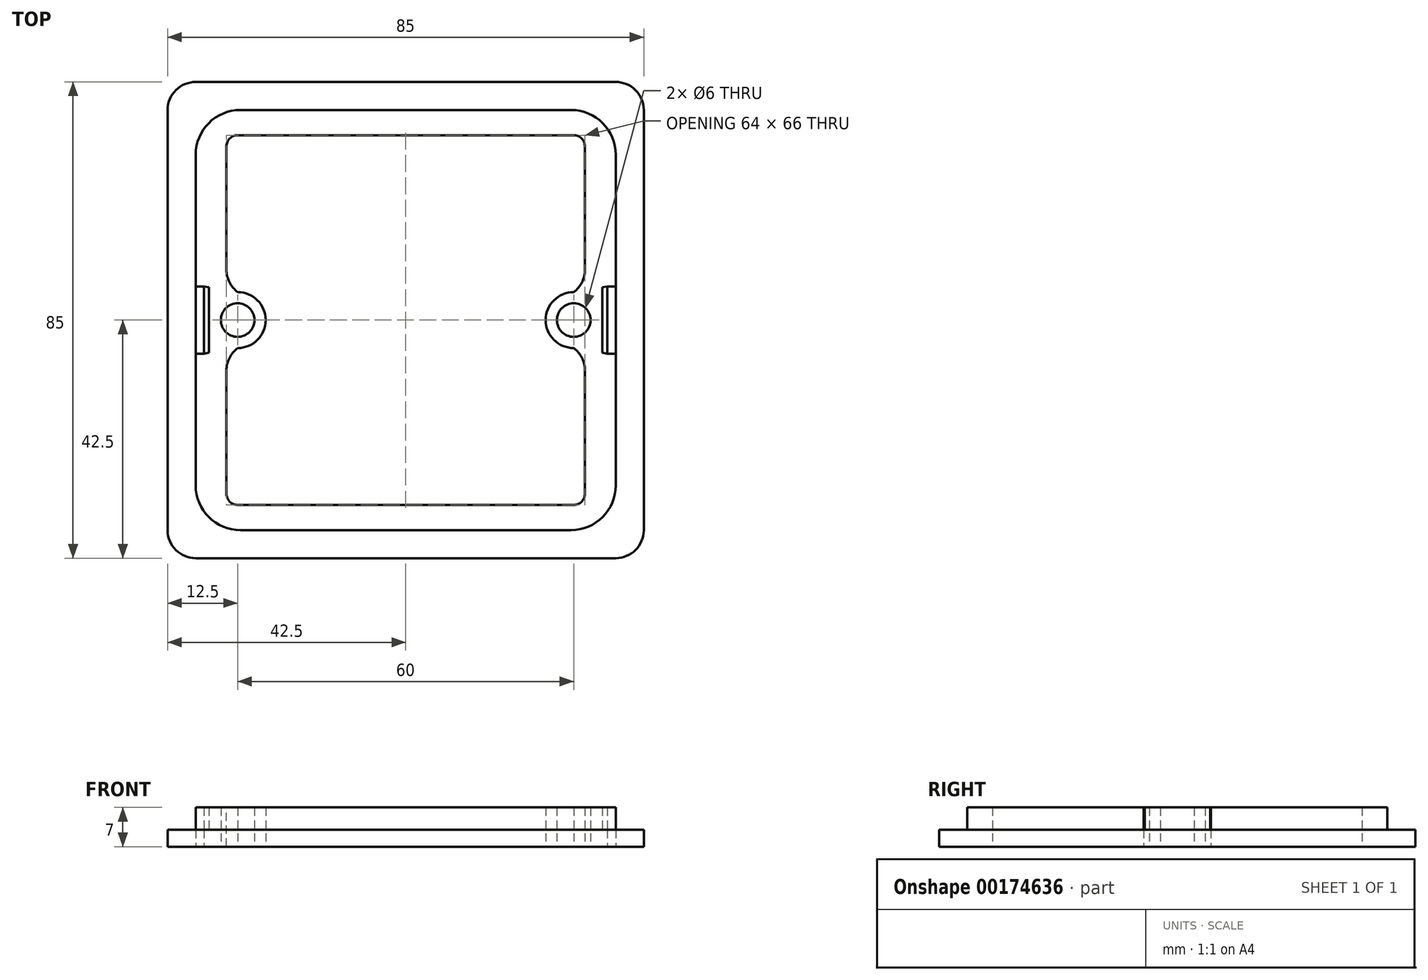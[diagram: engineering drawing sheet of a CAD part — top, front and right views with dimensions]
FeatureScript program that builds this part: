
annotation { "Feature Type Name" : "Feature", "Feature Type Description" : "" }
export const myFeature = defineFeature(function(context is Context, id is Id, definition is map)
    precondition{}
    {
        {
            var Q0;
            Q0=qCreatedBy(makeId("Top.planeOp"),FACE);
            var sketch = newSketch(context, id + "F0", { "sketchPlane" : qUnion([Q0])});
            skLineSegment(sketch, "E0.bottom", {"start": v(-42.5, 42.5) * mm, "end": v(42.5, 42.5) * mm});
            skLineSegment(sketch, "E0.top", {"start": v(-42.5, -42.5) * mm, "end": v(42.5, -42.5) * mm});
            skLineSegment(sketch, "E0.left", {"start": v(-42.5, 42.5) * mm, "end": v(-42.5, -42.5) * mm});
            skLineSegment(sketch, "E0.right", {"start": v(42.5, 42.5) * mm, "end": v(42.5, -42.5) * mm});
            skLineSegment(sketch, "E1.bottom", {"start": v(-32, 33) * mm, "end": v(32, 33) * mm});
            skLineSegment(sketch, "E1.top", {"start": v(-32, -33) * mm, "end": v(32, -33) * mm});
            skLineSegment(sketch, "E1.left", {"start": v(-32, 33) * mm, "end": v(-32, -33) * mm});
            skLineSegment(sketch, "E1.right", {"start": v(32, 33) * mm, "end": v(32, -33) * mm});
            skPoint(sketch, "E2", {"position": v(0, 33) * mm});
            skPoint(sketch, "E3", {"position": v(-42.5, 0) * mm});
            skPoint(sketch, "E4", {"position": v(-32, 0) * mm});
            skPoint(sketch, "E5", {"position": v(0, 42.5) * mm});
            skLineSegment(sketch, "E6.bottom", {"start": v(37.5, -37.5) * mm, "end": v(-37.5, -37.5) * mm});
            skLineSegment(sketch, "E6.top", {"start": v(37.5, 37.5) * mm, "end": v(-37.5, 37.5) * mm});
            skLineSegment(sketch, "E6.left", {"start": v(37.5, -37.5) * mm, "end": v(37.5, 37.5) * mm});
            skLineSegment(sketch, "E6.right", {"start": v(-37.5, -37.5) * mm, "end": v(-37.5, 37.5) * mm});
            skPoint(sketch, "E6.middle", {"position": v(0, 0) * mm});
            skCircle(sketch, "E7", {"center": v(-30, 0) * mm, "radius": 3 * mm});
            skLineSegment(sketch, "E8.bottom", {"start": v(35.1, 35.1) * mm, "end": v(-35.1, 35.1) * mm});
            skLineSegment(sketch, "E8.top", {"start": v(35.1, -35.1) * mm, "end": v(-35.1, -35.1) * mm});
            skLineSegment(sketch, "E8.left", {"start": v(35.1, 35.1) * mm, "end": v(35.1, -35.1) * mm});
            skLineSegment(sketch, "E8.right", {"start": v(-35.1, 35.1) * mm, "end": v(-35.1, -35.1) * mm});
            skLineSegment(sketch, "E9", {"start": v(0, 0) * mm, "end": v(0, 30.07) * mm});
            skCircle(sketch, "E10.MirrorC", {"center": v(30, 0) * mm, "radius": 3 * mm});
            skLineSegment(sketch, "E11.bottom", {"start": v(-37.5, 6) * mm, "end": v(-36, 6) * mm});
            skLineSegment(sketch, "E11.top", {"start": v(-37.5, -6) * mm, "end": v(-36, -6) * mm});
            skLineSegment(sketch, "E11.left", {"start": v(-37.5, 6) * mm, "end": v(-37.5, -6) * mm});
            skLineSegment(sketch, "E11.right", {"start": v(-36, 6) * mm, "end": v(-36, -6) * mm});
            skPoint(sketch, "E12", {"position": v(-36, 0) * mm});
            skLineSegment(sketch, "E13.MirrorCS", {"start": v(37.5, 6) * mm, "end": v(36, 6) * mm});
            skLineSegment(sketch, "E14.MirrorCS", {"start": v(37.5, -6) * mm, "end": v(36, -6) * mm});
            skLineSegment(sketch, "E15.MirrorCS", {"start": v(36, 6) * mm, "end": v(36, -6) * mm});
            skLineSegment(sketch, "E16.MirrorCS", {"start": v(37.5, 6) * mm, "end": v(37.5, -6) * mm});
            skCircle(sketch, "E17", {"center": v(-30, 0) * mm, "radius": 5 * mm});
            skLineSegment(sketch, "E18", {"start": v(-30, 5) * mm, "end": v(-36, 6) * mm});
            skLineSegment(sketch, "E19", {"start": v(-30, -5) * mm, "end": v(-36, -6) * mm});
            skLineSegment(sketch, "E20.MirrorCS", {"start": v(30, 5) * mm, "end": v(36, 6) * mm});
            skLineSegment(sketch, "E21.MirrorCS", {"start": v(30, -5) * mm, "end": v(36, -6) * mm});
            skCircle(sketch, "E22.MirrorC", {"center": v(30, 0) * mm, "radius": 5 * mm});
            skSolve(sketch);
        }
        {
            var Q0;
            Q0=makeQuery(id+"F0.imprint","IMPRINT",FACE,{"disambiguationData":[TD([[makeQuery(id+"F0.imprint","IMPRINT",EDGE,{"derivedFrom":sQuery(id+"F0.wireOp",EDGE,"E0.bottom")}),-1.0]])]});
            var Q1;
            {var subQ4=sQuery(id+"F0.wireOp",EDGE,"E6.bottom");Q1=makeQuery(id+"F0.imprint","IMPRINT",FACE,{"disambiguationData":[TD([[makeQuery(id+"F0.imprint","IMPRINT",EDGE,{"derivedFrom":subQ4}),-1.0]])]});}
            var Q2;
            {var subQ1=sQuery(id+"F0.wireOp",EDGE,"E6.top");Q2=makeQuery(id+"F0.imprint","IMPRINT",FACE,{"disambiguationData":[TD([[makeQuery(id+"F0.imprint","IMPRINT",EDGE,{"derivedFrom":subQ1}),1.0]])]});}
            var Q3;
            {var subQ2=sQuery(id+"F0.wireOp",EDGE,"E1.bottom");Q3=makeQuery(id+"F0.imprint","IMPRINT",FACE,{"disambiguationData":[TD([[makeQuery(id+"F0.imprint","IMPRINT",EDGE,{"derivedFrom":subQ2}),1.0]])]});}
            var Q4;
            {var subQ1=sQuery(id+"F0.wireOp",EDGE,"E1.left");var subQ8=sQuery(id+"F0.wireOp",EDGE,"E18");var subQ10=makeQuery(id+"F0.imprint","INTERSECT",VERTEX,{"derivedFrom":[subQ1,subQ8]});Q4=makeQuery(id+"F0.imprint","IMPRINT",FACE,{"disambiguationData":[TD([[makeQuery(id+"F0.imprint","IMPRINT",EDGE,{"disambiguationData":[TD([[subQ10,-1.0]])],"derivedFrom":subQ1}),-1.0]])]});}
            var Q5;
            {var subQ5=sQuery(id+"F0.wireOp",EDGE,"E11.right");Q5=makeQuery(id+"F0.imprint","IMPRINT",FACE,{"disambiguationData":[TD([[makeQuery(id+"F0.imprint","IMPRINT",EDGE,{"derivedFrom":subQ5}),1.0]])]});}
            var Q6;
            {var subQ0=sQuery(id+"F0.wireOp",EDGE,"E17");var subQ2=sQuery(id+"F0.wireOp",EDGE,"E1.left");var subQ3=makeQuery(id+"F0.imprint","INTERSECT",VERTEX,{"disambiguationData":[OD(0.0)],"derivedFrom":[subQ2,subQ0]});Q6=makeQuery(id+"F0.imprint","IMPRINT",FACE,{"disambiguationData":[TD([[makeQuery(id+"F0.imprint","IMPRINT",EDGE,{"disambiguationData":[TD([[subQ3,-1.0]])],"derivedFrom":subQ2}),1.0]])]});}
            var Q7;
            {var subQ0=sQuery(id+"F0.wireOp",EDGE,"E18");var subQ1=sQuery(id+"F0.wireOp",EDGE,"E1.left");var subQ2=makeQuery(id+"F0.imprint","INTERSECT",VERTEX,{"derivedFrom":[subQ1,subQ0]});Q7=makeQuery(id+"F0.imprint","IMPRINT",FACE,{"disambiguationData":[TD([[makeQuery(id+"F0.imprint","IMPRINT",EDGE,{"disambiguationData":[TD([[subQ2,-1.0]])],"derivedFrom":subQ1}),1.0]])]});}
            var Q8;
            {var subQ0=sQuery(id+"F0.wireOp",EDGE,"E17");var subQ1=sQuery(id+"F0.wireOp",EDGE,"E1.left");var subQ2=makeQuery(id+"F0.imprint","INTERSECT",VERTEX,{"disambiguationData":[OD(1.0)],"derivedFrom":[subQ1,subQ0]});Q8=makeQuery(id+"F0.imprint","IMPRINT",FACE,{"disambiguationData":[TD([[makeQuery(id+"F0.imprint","IMPRINT",EDGE,{"disambiguationData":[TD([[subQ2,-1.0]])],"derivedFrom":subQ1}),1.0]])]});}
            var Q9;
            {var subQ11=sQuery(id+"F0.wireOp",EDGE,"E1.top");Q9=makeQuery(id+"F0.imprint","IMPRINT",FACE,{"disambiguationData":[TD([[makeQuery(id+"F0.imprint","IMPRINT",EDGE,{"derivedFrom":subQ11}),-1.0]])]});}
            var Q10;
            {var subQ0=sQuery(id+"F0.wireOp",EDGE,"E20.MirrorCS");var subQ6=sQuery(id+"F0.wireOp",EDGE,"E1.right");var subQ9=makeQuery(id+"F0.imprint","INTERSECT",VERTEX,{"derivedFrom":[subQ6,subQ0]});Q10=makeQuery(id+"F0.imprint","IMPRINT",FACE,{"disambiguationData":[TD([[makeQuery(id+"F0.imprint","IMPRINT",EDGE,{"disambiguationData":[TD([[subQ9,-1.0]])],"derivedFrom":subQ6}),1.0]])]});}
            var Q11;
            {var subQ0=sQuery(id+"F0.wireOp",EDGE,"E20.MirrorCS");var subQ1=sQuery(id+"F0.wireOp",EDGE,"E1.right");var subQ2=makeQuery(id+"F0.imprint","INTERSECT",VERTEX,{"derivedFrom":[subQ1,subQ0]});Q11=makeQuery(id+"F0.imprint","IMPRINT",FACE,{"disambiguationData":[TD([[makeQuery(id+"F0.imprint","IMPRINT",EDGE,{"disambiguationData":[TD([[subQ2,-1.0]])],"derivedFrom":subQ1}),-1.0]])]});}
            var Q12;
            {var subQ0=sQuery(id+"F0.wireOp",EDGE,"E22.MirrorC");var subQ1=sQuery(id+"F0.wireOp",EDGE,"E1.right");var subQ2=makeQuery(id+"F0.imprint","INTERSECT",VERTEX,{"disambiguationData":[OD(1.0)],"derivedFrom":[subQ1,subQ0]});Q12=makeQuery(id+"F0.imprint","IMPRINT",FACE,{"disambiguationData":[TD([[makeQuery(id+"F0.imprint","IMPRINT",EDGE,{"disambiguationData":[TD([[subQ2,-1.0]])],"derivedFrom":subQ1}),-1.0]])]});}
            var Q13;
            {var subQ0=sQuery(id+"F0.wireOp",EDGE,"E22.MirrorC");var subQ2=sQuery(id+"F0.wireOp",EDGE,"E1.right");var subQ3=makeQuery(id+"F0.imprint","INTERSECT",VERTEX,{"disambiguationData":[OD(0.0)],"derivedFrom":[subQ2,subQ0]});Q13=makeQuery(id+"F0.imprint","IMPRINT",FACE,{"disambiguationData":[TD([[makeQuery(id+"F0.imprint","IMPRINT",EDGE,{"disambiguationData":[TD([[subQ3,-1.0]])],"derivedFrom":subQ2}),-1.0]])]});}
            var Q14;
            {var subQ0=sQuery(id+"F0.wireOp",EDGE,"E22.MirrorC");var subQ1=sQuery(id+"F0.wireOp",EDGE,"E1.right");var subQ2=makeQuery(id+"F0.imprint","INTERSECT",VERTEX,{"disambiguationData":[OD(0.0)],"derivedFrom":[subQ1,subQ0]});Q14=makeQuery(id+"F0.imprint","IMPRINT",FACE,{"disambiguationData":[TD([[makeQuery(id+"F0.imprint","IMPRINT",EDGE,{"disambiguationData":[TD([[subQ2,-1.0]])],"derivedFrom":subQ1}),1.0]])]});}
            var Q15;
            {var subQ0=sQuery(id+"F0.wireOp",EDGE,"E17");var subQ1=sQuery(id+"F0.wireOp",EDGE,"E1.left");var subQ2=makeQuery(id+"F0.imprint","INTERSECT",VERTEX,{"disambiguationData":[OD(0.0)],"derivedFrom":[subQ1,subQ0]});Q15=makeQuery(id+"F0.imprint","IMPRINT",FACE,{"disambiguationData":[TD([[makeQuery(id+"F0.imprint","IMPRINT",EDGE,{"disambiguationData":[TD([[subQ2,-1.0]])],"derivedFrom":subQ1}),-1.0]])]});}
            var Q16;
            {var subQ5=sQuery(id+"F0.wireOp",EDGE,"E15.MirrorCS");Q16=makeQuery(id+"F0.imprint","IMPRINT",FACE,{"disambiguationData":[TD([[makeQuery(id+"F0.imprint","IMPRINT",EDGE,{"derivedFrom":subQ5}),-1.0]])]});}
            extrude(context, id + "F1", {"entities" : qUnion([Q0, Q1, Q2, Q3, Q4, Q5, Q6, Q7, Q8, Q9, Q10, Q11, Q12, Q13, Q14, Q15, Q16]), "depth" : 3 * mm});
        }
        {
            var Q0;
            Q0=makeQuery(id+"F1.opExtrude","SWEPT_EDGE",EDGE,{"disambiguationData":[OSD([sQuery(id+"F0.wireOp",EDGE,"E0.bottom"),sQuery(id+"F0.wireOp",EDGE,"E0.left")])]});
            var Q1;
            Q1=makeQuery(id+"F1.opExtrude","SWEPT_EDGE",EDGE,{"disambiguationData":[OSD([sQuery(id+"F0.wireOp",EDGE,"E0.top"),sQuery(id+"F0.wireOp",EDGE,"E0.left")])]});
            var Q2;
            Q2=makeQuery(id+"F1.opExtrude","SWEPT_EDGE",EDGE,{"disambiguationData":[OSD([sQuery(id+"F0.wireOp",EDGE,"E0.top"),sQuery(id+"F0.wireOp",EDGE,"E0.right")])]});
            var Q3;
            Q3=makeQuery(id+"F1.opExtrude","SWEPT_EDGE",EDGE,{"disambiguationData":[OSD([sQuery(id+"F0.wireOp",EDGE,"E0.bottom"),sQuery(id+"F0.wireOp",EDGE,"E0.right")])]});
            fillet(context, id + "F2", {"entities" : qUnion([Q0, Q1, Q2, Q3]), "radius" : 5 * mm, "tangentPropagation" : true, "allowEdgeOverflow" : false});
        }
        {
            var Q0;
            {var subQ1=sQuery(id+"F0.wireOp",EDGE,"E1.left");var subQ8=sQuery(id+"F0.wireOp",EDGE,"E18");var subQ10=makeQuery(id+"F0.imprint","INTERSECT",VERTEX,{"derivedFrom":[subQ1,subQ8]});Q0=makeQuery(id+"F0.imprint","IMPRINT",FACE,{"disambiguationData":[TD([[makeQuery(id+"F0.imprint","IMPRINT",EDGE,{"disambiguationData":[TD([[subQ10,-1.0]])],"derivedFrom":subQ1}),-1.0]])]});}
            var Q1;
            {var subQ0=sQuery(id+"F0.wireOp",EDGE,"E18");var subQ1=sQuery(id+"F0.wireOp",EDGE,"E1.left");var subQ2=makeQuery(id+"F0.imprint","INTERSECT",VERTEX,{"derivedFrom":[subQ1,subQ0]});Q1=makeQuery(id+"F0.imprint","IMPRINT",FACE,{"disambiguationData":[TD([[makeQuery(id+"F0.imprint","IMPRINT",EDGE,{"disambiguationData":[TD([[subQ2,-1.0]])],"derivedFrom":subQ1}),1.0]])]});}
            var Q2;
            {var subQ0=sQuery(id+"F0.wireOp",EDGE,"E17");var subQ2=sQuery(id+"F0.wireOp",EDGE,"E1.left");var subQ3=makeQuery(id+"F0.imprint","INTERSECT",VERTEX,{"disambiguationData":[OD(0.0)],"derivedFrom":[subQ2,subQ0]});Q2=makeQuery(id+"F0.imprint","IMPRINT",FACE,{"disambiguationData":[TD([[makeQuery(id+"F0.imprint","IMPRINT",EDGE,{"disambiguationData":[TD([[subQ3,-1.0]])],"derivedFrom":subQ2}),1.0]])]});}
            var Q3;
            {var subQ0=sQuery(id+"F0.wireOp",EDGE,"E17");var subQ1=sQuery(id+"F0.wireOp",EDGE,"E1.left");var subQ2=makeQuery(id+"F0.imprint","INTERSECT",VERTEX,{"disambiguationData":[OD(0.0)],"derivedFrom":[subQ1,subQ0]});Q3=makeQuery(id+"F0.imprint","IMPRINT",FACE,{"disambiguationData":[TD([[makeQuery(id+"F0.imprint","IMPRINT",EDGE,{"disambiguationData":[TD([[subQ2,-1.0]])],"derivedFrom":subQ1}),-1.0]])]});}
            var Q4;
            {var subQ0=sQuery(id+"F0.wireOp",EDGE,"E17");var subQ1=sQuery(id+"F0.wireOp",EDGE,"E1.left");var subQ2=makeQuery(id+"F0.imprint","INTERSECT",VERTEX,{"disambiguationData":[OD(1.0)],"derivedFrom":[subQ1,subQ0]});Q4=makeQuery(id+"F0.imprint","IMPRINT",FACE,{"disambiguationData":[TD([[makeQuery(id+"F0.imprint","IMPRINT",EDGE,{"disambiguationData":[TD([[subQ2,-1.0]])],"derivedFrom":subQ1}),1.0]])]});}
            var Q5;
            {var subQ11=sQuery(id+"F0.wireOp",EDGE,"E1.top");Q5=makeQuery(id+"F0.imprint","IMPRINT",FACE,{"disambiguationData":[TD([[makeQuery(id+"F0.imprint","IMPRINT",EDGE,{"derivedFrom":subQ11}),-1.0]])]});}
            var Q6;
            {var subQ2=sQuery(id+"F0.wireOp",EDGE,"E6.bottom");Q6=makeQuery(id+"F0.imprint","IMPRINT",FACE,{"disambiguationData":[TD([[makeQuery(id+"F0.imprint","IMPRINT",EDGE,{"derivedFrom":subQ2}),-1.0]])]});}
            var Q7;
            {var subQ1=sQuery(id+"F0.wireOp",EDGE,"E6.top");Q7=makeQuery(id+"F0.imprint","IMPRINT",FACE,{"disambiguationData":[TD([[makeQuery(id+"F0.imprint","IMPRINT",EDGE,{"derivedFrom":subQ1}),1.0]])]});}
            var Q8;
            {var subQ2=sQuery(id+"F0.wireOp",EDGE,"E1.bottom");Q8=makeQuery(id+"F0.imprint","IMPRINT",FACE,{"disambiguationData":[TD([[makeQuery(id+"F0.imprint","IMPRINT",EDGE,{"derivedFrom":subQ2}),1.0]])]});}
            var Q9;
            {var subQ0=sQuery(id+"F0.wireOp",EDGE,"E22.MirrorC");var subQ1=sQuery(id+"F0.wireOp",EDGE,"E1.right");var subQ2=makeQuery(id+"F0.imprint","INTERSECT",VERTEX,{"disambiguationData":[OD(1.0)],"derivedFrom":[subQ1,subQ0]});Q9=makeQuery(id+"F0.imprint","IMPRINT",FACE,{"disambiguationData":[TD([[makeQuery(id+"F0.imprint","IMPRINT",EDGE,{"disambiguationData":[TD([[subQ2,-1.0]])],"derivedFrom":subQ1}),-1.0]])]});}
            var Q10;
            {var subQ0=sQuery(id+"F0.wireOp",EDGE,"E22.MirrorC");var subQ2=sQuery(id+"F0.wireOp",EDGE,"E1.right");var subQ3=makeQuery(id+"F0.imprint","INTERSECT",VERTEX,{"disambiguationData":[OD(0.0)],"derivedFrom":[subQ2,subQ0]});Q10=makeQuery(id+"F0.imprint","IMPRINT",FACE,{"disambiguationData":[TD([[makeQuery(id+"F0.imprint","IMPRINT",EDGE,{"disambiguationData":[TD([[subQ3,-1.0]])],"derivedFrom":subQ2}),-1.0]])]});}
            var Q11;
            {var subQ0=sQuery(id+"F0.wireOp",EDGE,"E20.MirrorCS");var subQ1=sQuery(id+"F0.wireOp",EDGE,"E1.right");var subQ2=makeQuery(id+"F0.imprint","INTERSECT",VERTEX,{"derivedFrom":[subQ1,subQ0]});Q11=makeQuery(id+"F0.imprint","IMPRINT",FACE,{"disambiguationData":[TD([[makeQuery(id+"F0.imprint","IMPRINT",EDGE,{"disambiguationData":[TD([[subQ2,-1.0]])],"derivedFrom":subQ1}),-1.0]])]});}
            var Q12;
            {var subQ0=sQuery(id+"F0.wireOp",EDGE,"E22.MirrorC");var subQ1=sQuery(id+"F0.wireOp",EDGE,"E1.right");var subQ2=makeQuery(id+"F0.imprint","INTERSECT",VERTEX,{"disambiguationData":[OD(0.0)],"derivedFrom":[subQ1,subQ0]});Q12=makeQuery(id+"F0.imprint","IMPRINT",FACE,{"disambiguationData":[TD([[makeQuery(id+"F0.imprint","IMPRINT",EDGE,{"disambiguationData":[TD([[subQ2,-1.0]])],"derivedFrom":subQ1}),1.0]])]});}
            var Q13;
            {var subQ0=sQuery(id+"F0.wireOp",EDGE,"E20.MirrorCS");var subQ6=sQuery(id+"F0.wireOp",EDGE,"E1.right");var subQ9=makeQuery(id+"F0.imprint","INTERSECT",VERTEX,{"derivedFrom":[subQ6,subQ0]});Q13=makeQuery(id+"F0.imprint","IMPRINT",FACE,{"disambiguationData":[TD([[makeQuery(id+"F0.imprint","IMPRINT",EDGE,{"disambiguationData":[TD([[subQ9,-1.0]])],"derivedFrom":subQ6}),1.0]])]});}
            extrude(context, id + "F3", {"entities" : qUnion([Q0, Q1, Q2, Q3, Q4, Q5, Q6, Q7, Q8, Q9, Q10, Q11, Q12, Q13]), "operationType" : NewBodyOperationType.ADD, "depth" : 7 * mm});
        }
        {
            var Q0;
            Q0=makeQuery(id+"F3.opExtrude","SWEPT_EDGE",EDGE,{"disambiguationData":[OSD([sQuery(id+"F0.wireOp",EDGE,"E6.bottom"),sQuery(id+"F0.wireOp",EDGE,"E6.right")])]});
            var Q1;
            Q1=makeQuery(id+"F3.opExtrude","SWEPT_EDGE",EDGE,{"disambiguationData":[OSD([sQuery(id+"F0.wireOp",EDGE,"E6.bottom"),sQuery(id+"F0.wireOp",EDGE,"E6.left")])]});
            var Q2;
            Q2=makeQuery(id+"F3.opExtrude","SWEPT_EDGE",EDGE,{"disambiguationData":[OSD([sQuery(id+"F0.wireOp",EDGE,"E6.top"),sQuery(id+"F0.wireOp",EDGE,"E6.left")])]});
            var Q3;
            Q3=makeQuery(id+"F3.opExtrude","SWEPT_EDGE",EDGE,{"disambiguationData":[OSD([sQuery(id+"F0.wireOp",EDGE,"E6.top"),sQuery(id+"F0.wireOp",EDGE,"E6.right")])]});
            fillet(context, id + "F4", {"entities" : qUnion([Q0, Q1, Q2, Q3]), "radius" : 8 * mm, "tangentPropagation" : true, "allowEdgeOverflow" : false});
        }
        {
            var Q0;
            {var subQ0=sQuery(id+"F0.wireOp",EDGE,"E1.right");var subQ1=sQuery(id+"F0.wireOp",EDGE,"E1.top");Q0=makeQuery(id+"F3.boolean.opBoolean","MERGE",EDGE,{"derivedFrom":[makeQuery(id+"F1.opExtrude","SWEPT_EDGE",EDGE,{"disambiguationData":[OSD([subQ1,subQ0])]}),makeQuery(id+"F3.opExtrude","SWEPT_EDGE",EDGE,{"disambiguationData":[OSD([subQ1,subQ0])]})]});}
            var Q1;
            {var subQ0=sQuery(id+"F0.wireOp",EDGE,"E1.left");var subQ1=sQuery(id+"F0.wireOp",EDGE,"E1.top");Q1=makeQuery(id+"F3.boolean.opBoolean","MERGE",EDGE,{"derivedFrom":[makeQuery(id+"F1.opExtrude","SWEPT_EDGE",EDGE,{"disambiguationData":[OSD([subQ1,subQ0])]}),makeQuery(id+"F3.opExtrude","SWEPT_EDGE",EDGE,{"disambiguationData":[OSD([subQ1,subQ0])]})]});}
            var Q2;
            {var subQ0=sQuery(id+"F0.wireOp",EDGE,"E1.left");var subQ1=sQuery(id+"F0.wireOp",EDGE,"E1.bottom");Q2=makeQuery(id+"F3.boolean.opBoolean","MERGE",EDGE,{"derivedFrom":[makeQuery(id+"F1.opExtrude","SWEPT_EDGE",EDGE,{"disambiguationData":[OSD([subQ1,subQ0])]}),makeQuery(id+"F3.opExtrude","SWEPT_EDGE",EDGE,{"disambiguationData":[OSD([subQ1,subQ0])]})]});}
            var Q3;
            {var subQ0=sQuery(id+"F0.wireOp",EDGE,"E1.right");var subQ1=sQuery(id+"F0.wireOp",EDGE,"E1.bottom");Q3=makeQuery(id+"F3.boolean.opBoolean","MERGE",EDGE,{"derivedFrom":[makeQuery(id+"F1.opExtrude","SWEPT_EDGE",EDGE,{"disambiguationData":[OSD([subQ1,subQ0])]}),makeQuery(id+"F3.opExtrude","SWEPT_EDGE",EDGE,{"disambiguationData":[OSD([subQ1,subQ0])]})]});}
            fillet(context, id + "F5", {"entities" : qUnion([Q0, Q1, Q2, Q3]), "radius" : 2 * mm, "tangentPropagation" : true, "allowEdgeOverflow" : false});
        }
        {
            var Q0;
            {var subQ0=sQuery(id+"F0.wireOp",EDGE,"E21.MirrorCS");var subQ1=sQuery(id+"F0.wireOp",EDGE,"E1.right");Q0=makeQuery(id+"F3.boolean.opBoolean","MERGE",EDGE,{"derivedFrom":[makeQuery(id+"F1.opExtrude","SWEPT_EDGE",EDGE,{"disambiguationData":[OSD([subQ1,subQ0])]}),makeQuery(id+"F3.opExtrude","SWEPT_EDGE",EDGE,{"disambiguationData":[OSD([subQ1,subQ0])]})]});}
            var Q1;
            {var subQ0=sQuery(id+"F0.wireOp",EDGE,"E20.MirrorCS");var subQ1=sQuery(id+"F0.wireOp",EDGE,"E1.right");Q1=makeQuery(id+"F3.boolean.opBoolean","MERGE",EDGE,{"derivedFrom":[makeQuery(id+"F1.opExtrude","SWEPT_EDGE",EDGE,{"disambiguationData":[OSD([subQ1,subQ0])]}),makeQuery(id+"F3.opExtrude","SWEPT_EDGE",EDGE,{"disambiguationData":[OSD([subQ1,subQ0])]})]});}
            var Q2;
            {var subQ0=sQuery(id+"F0.wireOp",EDGE,"E18");var subQ1=sQuery(id+"F0.wireOp",EDGE,"E1.left");Q2=makeQuery(id+"F3.boolean.opBoolean","MERGE",EDGE,{"derivedFrom":[makeQuery(id+"F1.opExtrude","SWEPT_EDGE",EDGE,{"disambiguationData":[OSD([subQ1,subQ0])]}),makeQuery(id+"F3.opExtrude","SWEPT_EDGE",EDGE,{"disambiguationData":[OSD([subQ1,subQ0])]})]});}
            var Q3;
            {var subQ0=sQuery(id+"F0.wireOp",EDGE,"E19");var subQ1=sQuery(id+"F0.wireOp",EDGE,"E1.left");Q3=makeQuery(id+"F3.boolean.opBoolean","MERGE",EDGE,{"derivedFrom":[makeQuery(id+"F1.opExtrude","SWEPT_EDGE",EDGE,{"disambiguationData":[OSD([subQ1,subQ0])]}),makeQuery(id+"F3.opExtrude","SWEPT_EDGE",EDGE,{"disambiguationData":[OSD([subQ1,subQ0])]})]});}
            fillet(context, id + "F6", {"entities" : qUnion([Q0, Q1, Q2, Q3]), "radius" : 5 * mm, "tangentPropagation" : true, "allowEdgeOverflow" : false});
        }
    });
